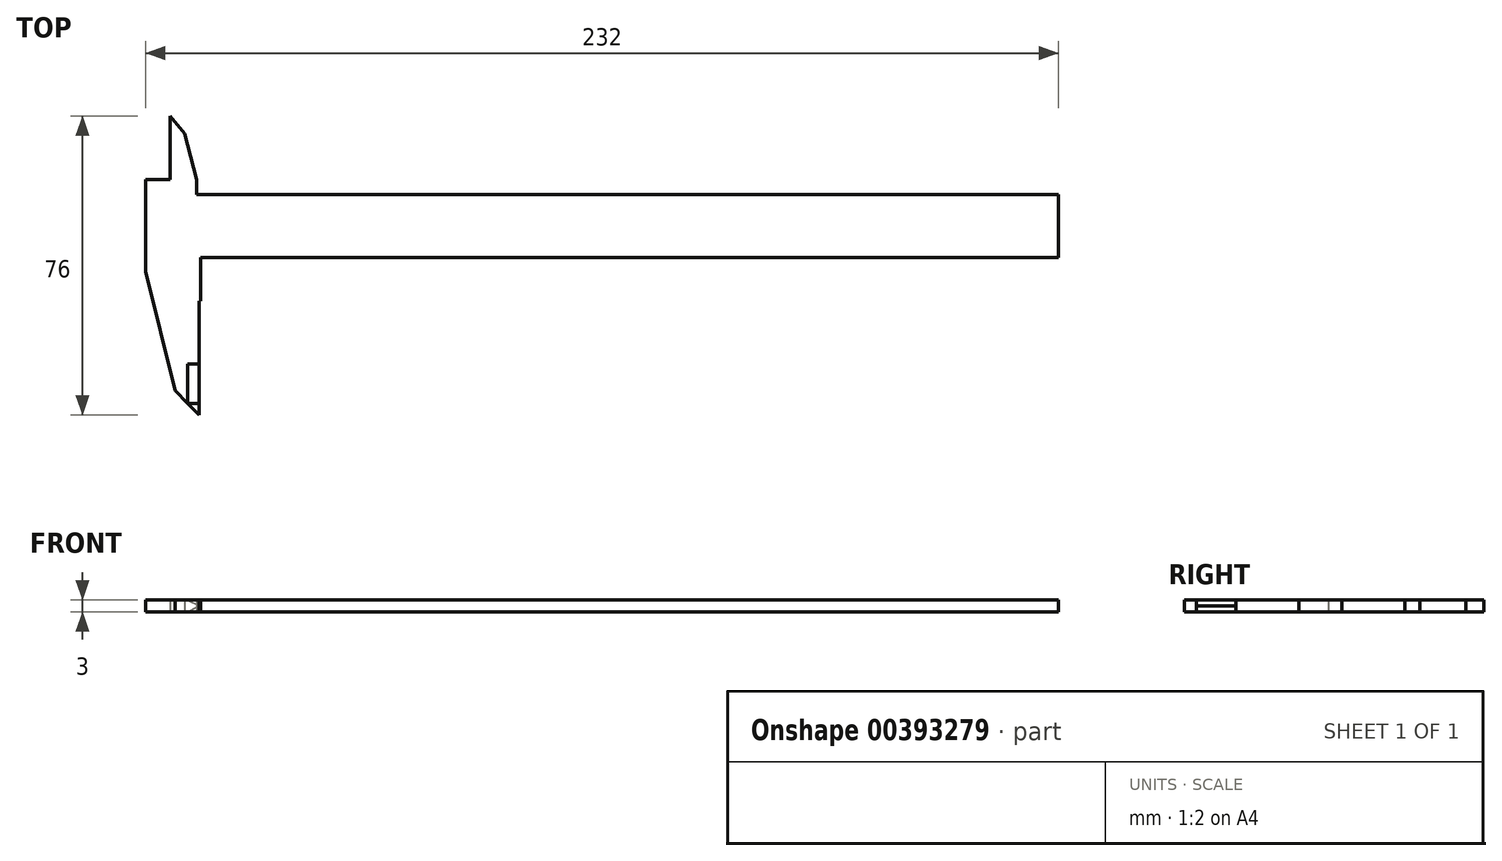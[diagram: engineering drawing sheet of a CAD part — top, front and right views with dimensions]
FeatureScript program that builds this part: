
annotation { "Feature Type Name" : "Feature", "Feature Type Description" : "" }
export const myFeature = defineFeature(function(context is Context, id is Id, definition is map)
    precondition{}
    {
        {
            var Q0;
            Q0=qCreatedBy(makeId("Top.planeOp"),FACE);
            var sketch = newSketch(context, id + "F0", { "sketchPlane" : qUnion([Q0])});
            skLineSegment(sketch, "E0.bottom", {"start": v(0, 0) * mm, "end": v(-219, 0) * mm});
            skLineSegment(sketch, "E0.top", {"start": v(0, -16) * mm, "end": v(-218, -16) * mm});
            skLineSegment(sketch, "E0.left", {"start": v(0, 0) * mm, "end": v(0, -16) * mm});
            skLineSegment(sketch, "E1", {"start": v(-232, -19.5) * mm, "end": v(-224.5, -49.8) * mm});
            skLineSegment(sketch, "E2", {"start": v(-224.5, -49.8) * mm, "end": v(-218.3, -56) * mm});
            skLineSegment(sketch, "E3", {"start": v(-218.3, -56) * mm, "end": v(-218.3, -27) * mm});
            skLineSegment(sketch, "E4", {"start": v(-218, -27) * mm, "end": v(-218.3, -27) * mm});
            skLineSegment(sketch, "E5", {"start": v(-218, -27) * mm, "end": v(-218, -16) * mm});
            skLineSegment(sketch, "E6", {"start": v(-232, -19.5) * mm, "end": v(-232, 3.8) * mm});
            skLineSegment(sketch, "E7", {"start": v(-219, 3.8) * mm, "end": v(-219, 0) * mm});
            skLineSegment(sketch, "E8", {"start": v(-225.7, 20) * mm, "end": v(-225.7, 3.8) * mm});
            skLineSegment(sketch, "E9", {"start": v(-225.7, 3.8) * mm, "end": v(-232, 3.8) * mm});
            skLineSegment(sketch, "E10", {"start": v(-225.7, 20) * mm, "end": v(-222.04, 15.5) * mm});
            skLineSegment(sketch, "E11", {"start": v(-222.04, 15.5) * mm, "end": v(-219, 3.8) * mm});
            skSolve(sketch);
        }
        {
            var Q0;
            Q0=makeQuery(id+"F0.imprint","IMPRINT",FACE,{"disambiguationData":[TD([[makeQuery(id+"F0.imprint","IMPRINT",EDGE,{"derivedFrom":sQuery(id+"F0.wireOp",EDGE,"E0.bottom")}),1.0]])]});
            var Q1;
            {var subQ2=sQuery(id+"F0.wireOp",EDGE,"kT5vSTM3-CrME-x13C-qBvZ-SphoOoy0UPiU");Q1=makeQuery(id+"F0.imprint","IMPRINT",FACE,{"disambiguationData":[TD([[makeQuery(id+"F0.imprint","IMPRINT",EDGE,{"derivedFrom":subQ2}),-1.0]])]});}
            extrude(context, id + "F1", {"entities" : qUnion([Q0, Q1]), "depth" : 3 * mm});
        }
        {
            var Q0;
            Q0=qCreatedBy(makeId("Front.planeOp"),FACE);
            cPlane(context, id + "F2", {"entities" : qUnion([Q0]), "cplaneType" : CPlaneType.OFFSET, "offset" : 53 * mm, "width" : 150 * mm, "height" : 150 * mm});
        }
        {
            var Q0;
            Q0=qCreatedBy(id+"F2.planeOp",FACE);
            var sketch = newSketch(context, id + "F3", { "sketchPlane" : qUnion([Q0])});
            skLineSegment(sketch, "E12", {"start": v(-218.3, 1.5) * mm, "end": v(-221.3, 3) * mm});
            skLineSegment(sketch, "E13", {"start": v(-221.3, 3) * mm, "end": v(-213.3, 3) * mm});
            skLineSegment(sketch, "E14", {"start": v(-213.3, 3) * mm, "end": v(-213.3, 0) * mm});
            skLineSegment(sketch, "E15", {"start": v(-213.3, 0) * mm, "end": v(-221.3, 0) * mm});
            skLineSegment(sketch, "E16", {"start": v(-221.3, 0) * mm, "end": v(-218.3, 1.5) * mm});
            skSolve(sketch);
        }
        {
            var Q0;
            Q0=makeQuery(id+"F3.imprint","IMPRINT",FACE,{"disambiguationData":[TD([[makeQuery(id+"F3.imprint","IMPRINT",EDGE,{"derivedFrom":sQuery(id+"F3.wireOp",EDGE,"E12")}),-1.0]])]});
            extrude(context, id + "F4", {"entities" : qUnion([Q0]), "operationType" : NewBodyOperationType.REMOVE, "oppositeDirection" : true, "depth" : 10 * mm});
        }
    });
